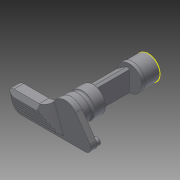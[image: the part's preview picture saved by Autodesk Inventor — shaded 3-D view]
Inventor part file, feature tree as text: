
AUTODESK INVENTOR PART (.ipt)
format: ipt  version: 2014 SP2 (Build 180246200, 246)  size: 270,336 bytes
history: native  units: in
note: dims shown in document units (in); Inventor stores cm internally (conversion verified against a paired STEP export)
features: sketch x11, extrude x8, projected_geometry x6, plane x3, revolve x2, other x1, sweep x1
ambient origin geometry x8: Origin, YZ Plane, XZ Plane, XY Plane, X Axis, Y Axis, Z Axis, Center Point
bodies: Solid1 (feature_tree)
feature tree (32):
  other  "Takedown Lever"
  extrude  "Extrusion1"  Depth=0.0035in
  extrude  "Extrusion2"  Depth=0.3779in
  extrude  "Extrusion3"  Depth=0.3095in
  revolve  "Revolution1"  Angle=75.0deg
  revolve  "Revolution2"  [1 undecoded]
  plane  "Work Plane1"
  extrude  "Extrusion4"  Depth=1.068in TaperAngle=0.0deg
  extrude  "Extrusion5"  Depth=0.031in
  sweep  "Sweep1"
  plane  "Work Plane2"
  extrude  "Extrusion6"  TaperAngle=90.0deg  [1 undecoded]
  plane  "Work Plane3"
  extrude  "Extrusion7"  Depth=0.3937in
  extrude  "Extrusion8"  TaperAngle=90.0deg  [1 undecoded]
  sketch  "Sketch1"  dims[d1=0.483in d2=0.0035in]
  sketch  "Sketch2"  dims[d3=0.35in d4=0.3779in]
  sketch  "Sketch3"  dims[d5=0.0781in d6=0.3095in]
  projected_geometry  "Projected Loop1"
  sketch  "Sketch4"  dims[d7=0.1875in d8=75.0deg]
  sketch  "Sketch5"  dims[d9=0.0781in d10=1.1in]
  sketch  "Sketch6"  dims[d11=0.086in d12=0.0in d13=1.068in d14=0.0in]
  sketch  "Sketch7"  dims[d15=0.0955in d16=0.031in]
  projected_geometry  "Projected Loop2"
  sketch  "Sketch8"  dims[d17=0.0785in d18=0.0in d19=0.06in]
  projected_geometry  "Projected Loop3"
  sketch  "3D Sketch1"
  sketch  "Sketch11"  dims[d21=0.1785in d22=90.0deg]
  sketch  "Sketch12"  dims[d23=0.3315in d24=0.2125in d25=90.0deg d26=-0.3875in d27=0.1775in d28=0.3779in d29=0.264in d30=0.298in d31=0.5045in d32=0.0in d33=0.481in d34=0.0795in d35=0.0in d36=0.0in d37=0.0715in d38=0.031in d39=2.3622in d41=0.0397in d42=0.3937in d44=1.0in d46=2.3622in d48=0.0133in d49=0.3937in d51=1.0in d53=0.0795in d54=0.0in d55=90.0deg d56=1.0in d57=0.0in d58=0.045in d59=0.0in]
  projected_geometry  "Project Cut Edges1"
  projected_geometry  "Project Cut Edges2"
  projected_geometry  "Project Cut Edges3"
note: 3 required parameter values undecoded (feature->parameter linkage not recoverable at this tier; creation-order binding heuristic only, values carry confidence <= 0.55)